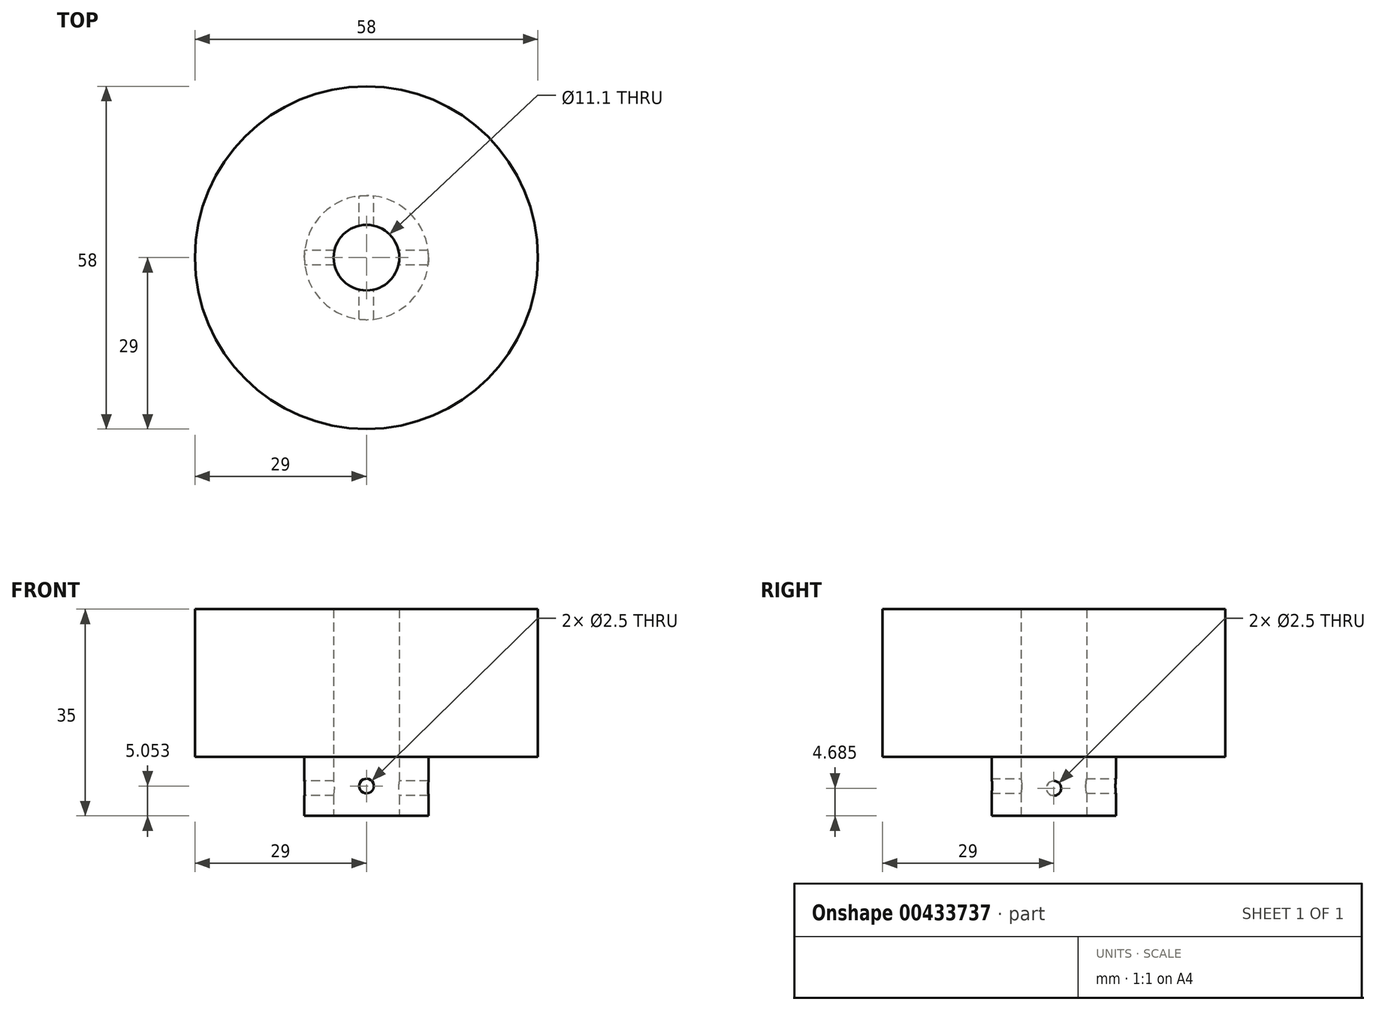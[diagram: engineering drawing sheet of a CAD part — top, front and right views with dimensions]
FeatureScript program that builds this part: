
annotation { "Feature Type Name" : "Feature", "Feature Type Description" : "" }
export const myFeature = defineFeature(function(context is Context, id is Id, definition is map)
    precondition{}
    {
        {
            var Q0;
            Q0=qCreatedBy(makeId("Top.planeOp"),FACE);
            var sketch = newSketch(context, id + "F0", { "sketchPlane" : qUnion([Q0])});
            skCircle(sketch, "E0", {"center": v(0, 0) * mm, "radius": 29 * mm});
            skSolve(sketch);
        }
        {
            var Q0;
            Q0=makeQuery(id+"F0.imprint","IMPRINT",FACE,{"disambiguationData":[TD([[makeQuery(id+"F0.imprint","IMPRINT",EDGE,{"derivedFrom":sQuery(id+"F0.wireOp",EDGE,"E0")}),1.0]])]});
            extrude(context, id + "F1", {"entities" : qUnion([Q0]), "depth" : 25 * mm});
        }
        {
            var Q0;
            Q0=makeQuery(id+"F1.opExtrude","CAP_FACE",FACE,{"disambiguationData":[OSD([sQuery(id+"F0.wireOp",EDGE,"E0")])],"isStart":true});
            var sketch = newSketch(context, id + "F2", { "sketchPlane" : qUnion([Q0])});
            skCircle(sketch, "E1", {"center": v(0, 0) * mm, "radius": 10.5 * mm});
            skSolve(sketch);
        }
        {
            var Q0;
            Q0 = qSketchRegion(id + "F2", true);
            extrude(context, id + "F3", {"entities" : qUnion([Q0]), "operationType" : NewBodyOperationType.ADD, "depth" : 10 * mm});
        }
        {
            var Q0;
            Q0=makeQuery(id+"F3.opExtrude","CAP_FACE",FACE,{"disambiguationData":[OSD([sQuery(id+"F2.wireOp",EDGE,"E1")])],"isStart":false});
            var sketch = newSketch(context, id + "F4", { "sketchPlane" : qUnion([Q0])});
            skCircle(sketch, "E2", {"center": v(0, 0) * mm, "radius": 5.55 * mm});
            skSolve(sketch);
        }
        {
            var Q0;
            Q0=sQuery(id+"F4.wireOp",VERTEX,"E2.center");
            var Q1;
            Q1=makeQuery(id+"F1.opExtrude","SWEPT_BODY",BODY,{"disambiguationData":[OSD([sQuery(id+"F0.wireOp",EDGE,"E0")])]});
            hole(context, id + "F5", {"style" : HoleStyle.SIMPLE, "endStyle" : HoleEndStyle.THROUGH, "holeDiameter" : 11.1 * mm, "isTappedThrough" : true, "tappedDepth" : 12 * mm, "tapClearance" : 3, "locations" : qUnion([Q0]), "scope" : qUnion([Q1])});
        }
        {
            var Q0;
            Q0=makeQuery(id+"F3.opExtrude","CAP_EDGE",EDGE,{"disambiguationData":[OSD([sQuery(id+"F2.wireOp",EDGE,"E1")])],"isStart":false});
            cPlane(context, id + "F6", {"entities" : qUnion([Q0]), "cplaneType" : CPlaneType.LINE_ANGLE, "offset" : 25 * mm, "angle" : 0 * degree, "width" : 150 * mm, "height" : 150 * mm});
        }
        {
            var Q0;
            Q0=qCreatedBy(id+"F6.planeOp",FACE);
            cPlane(context, id + "F7", {"entities" : qUnion([Q0]), "cplaneType" : CPlaneType.OFFSET, "offset" : 10.5 * mm, "width" : 150 * mm, "height" : 150 * mm});
        }
        {
            var Q0;
            Q0=qCreatedBy(id+"F7.planeOp",FACE);
            var sketch = newSketch(context, id + "F8", { "sketchPlane" : qUnion([Q0])});
            skCircle(sketch, "E3", {"center": v(0, -5.32) * mm, "radius": 1.35 * mm});
            skSolve(sketch);
        }
        {
            var Q0;
            Q0=sQuery(id+"F8.wireOp",VERTEX,"E3.center");
            var Q1;
            Q1=makeQuery(id+"F1.opExtrude","SWEPT_BODY",BODY,{"disambiguationData":[OSD([sQuery(id+"F0.wireOp",EDGE,"E0")])]});
            hole(context, id + "F9", {"style" : HoleStyle.SIMPLE, "endStyle" : HoleEndStyle.THROUGH, "holeDiameter" : 2.5 * mm, "isTappedThrough" : true, "tappedDepth" : 12 * mm, "tapClearance" : 3, "locations" : qUnion([Q0]), "scope" : qUnion([Q1])});
        }
        {
            var Q0;
            Q0=makeQuery(id+"F3.opExtrude","CAP_EDGE",EDGE,{"disambiguationData":[OSD([sQuery(id+"F2.wireOp",EDGE,"E1")])],"isStart":false});
            cPlane(context, id + "F10", {"entities" : qUnion([Q0]), "cplaneType" : CPlaneType.LINE_ANGLE, "offset" : 25 * mm, "angle" : 90 * degree, "width" : 150 * mm, "height" : 150 * mm});
        }
        {
            var Q0;
            Q0=qCreatedBy(id+"F10.planeOp",FACE);
            cPlane(context, id + "F11", {"entities" : qUnion([Q0]), "cplaneType" : CPlaneType.OFFSET, "offset" : 10.5 * mm, "width" : 150 * mm, "height" : 150 * mm});
        }
        {
            var Q0;
            Q0=qCreatedBy(id+"F11.planeOp",FACE);
            var sketch = newSketch(context, id + "F12", { "sketchPlane" : qUnion([Q0])});
            skCircle(sketch, "E4", {"center": v(0, -4.95) * mm, "radius": 1.25 * mm});
            skSolve(sketch);
        }
        {
            var Q0;
            Q0=sQuery(id+"F12.wireOp",VERTEX,"E4.center");
            var Q1;
            Q1=makeQuery(id+"F1.opExtrude","SWEPT_BODY",BODY,{"disambiguationData":[OSD([sQuery(id+"F0.wireOp",EDGE,"E0")])]});
            hole(context, id + "F13", {"style" : HoleStyle.SIMPLE, "endStyle" : HoleEndStyle.THROUGH, "holeDiameter" : 2.5 * mm, "isTappedThrough" : true, "tappedDepth" : 12 * mm, "tapClearance" : 3, "locations" : qUnion([Q0]), "scope" : qUnion([Q1])});
        }
    });
